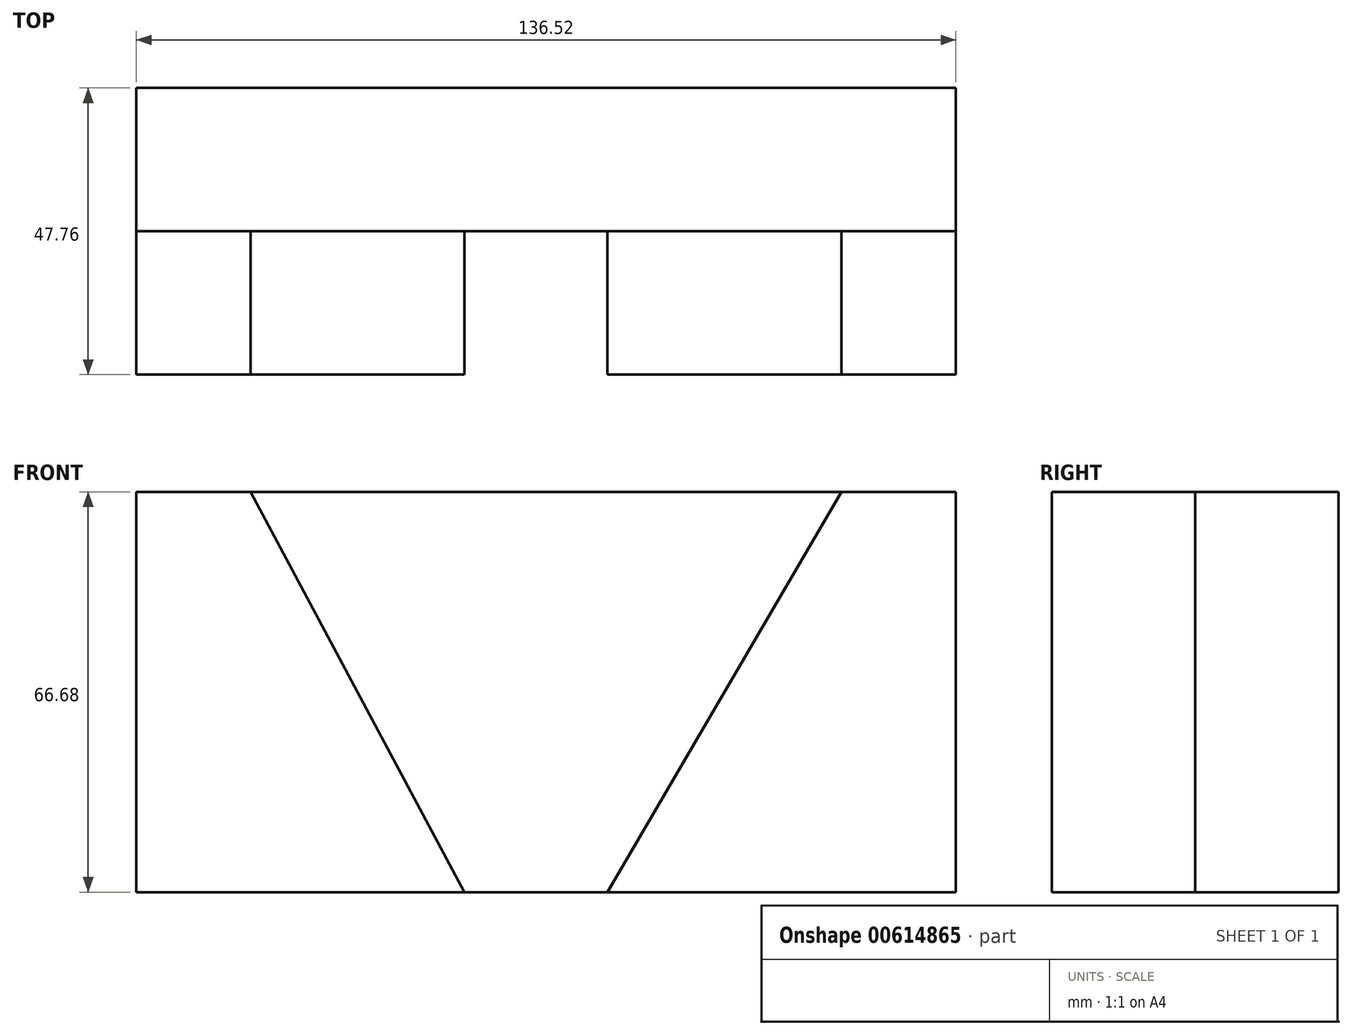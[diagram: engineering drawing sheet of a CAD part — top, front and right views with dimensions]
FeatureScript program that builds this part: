
annotation { "Feature Type Name" : "Feature", "Feature Type Description" : "" }
export const myFeature = defineFeature(function(context is Context, id is Id, definition is map)
    precondition{}
    {
        {
            var Q0;
            Q0=qCreatedBy(makeId("Front.planeOp"),FACE);
            var sketch = newSketch(context, id + "F0", { "sketchPlane" : qUnion([Q0])});
            skLineSegment(sketch, "E0.bottom", {"start": v(68.26, 33.34) * mm, "end": v(-68.26, 33.34) * mm});
            skLineSegment(sketch, "E0.top", {"start": v(68.26, -33.34) * mm, "end": v(-68.26, -33.34) * mm});
            skLineSegment(sketch, "E0.left", {"start": v(68.26, 33.34) * mm, "end": v(68.26, -33.34) * mm});
            skLineSegment(sketch, "E0.right", {"start": v(-68.26, 33.34) * mm, "end": v(-68.26, -33.34) * mm});
            skPoint(sketch, "E0.middle", {"position": v(0, 0) * mm});
            skPoint(sketch, "E1", {"position": v(49.21, 33.34) * mm});
            skPoint(sketch, "E2", {"position": v(-49.21, 33.34) * mm});
            skLineSegment(sketch, "E3", {"start": v(-49.21, 33.34) * mm, "end": v(-13.59, -33.34) * mm});
            skLineSegment(sketch, "E4", {"start": v(49.21, 33.34) * mm, "end": v(10.22, -33.34) * mm});
            skLineSegment(sketch, "E5.left", {"start": v(68.26, 33.34) * mm, "end": v(68.26, -33.13) * mm});
            skSolve(sketch);
        }
        {
            var Q0;
            {var subQ0=sQuery(id+"F0.wireOp",EDGE,"E0.right");Q0=makeQuery(id+"F0.imprint","IMPRINT",FACE,{"disambiguationData":[TD([[makeQuery(id+"F0.imprint","IMPRINT",EDGE,{"derivedFrom":subQ0}),1.0]])]});}
            var Q1;
            {var subQ1=sQuery(id+"F0.wireOp",EDGE,"E0.left");Q1=makeQuery(id+"F0.imprint","IMPRINT",FACE,{"disambiguationData":[TD([[makeQuery(id+"F0.imprint","IMPRINT",EDGE,{"derivedFrom":subQ1}),-1.0]])]});}
            extrude(context, id + "F1", {"entities" : qUnion([Q0, Q1]), "depth" : 23.88 * mm, "offsetDistance" : 25.4 * mm});
        }
        {
            var Q0;
            Q0 = qSketchRegion(id + "F0", true);
            extrude(context, id + "F2", {"entities" : qUnion([Q0]), "oppositeDirection" : true, "depth" : 23.88 * mm, "offsetDistance" : 25.4 * mm});
        }
    });
